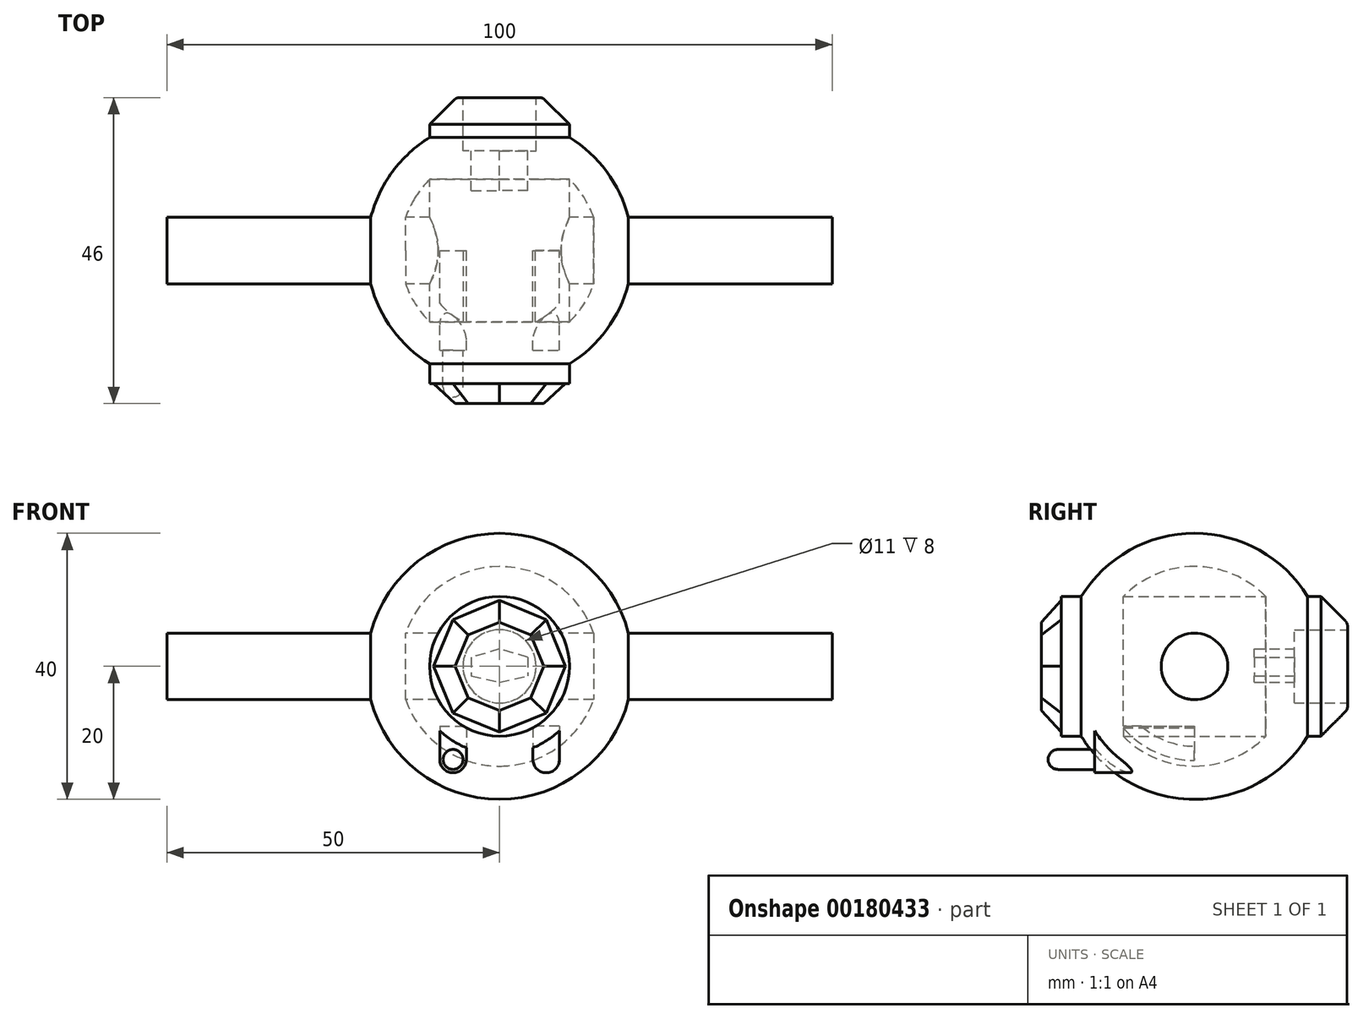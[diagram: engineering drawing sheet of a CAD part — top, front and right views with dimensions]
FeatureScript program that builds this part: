
annotation { "Feature Type Name" : "Feature", "Feature Type Description" : "" }
export const myFeature = defineFeature(function(context is Context, id is Id, definition is map)
    precondition{}
    {
        {
            var Q0;
            Q0=qCreatedBy(makeId("Front.planeOp"),FACE);
            var sketch = newSketch(context, id + "F0", { "sketchPlane" : qUnion([Q0])});
            skArc(sketch, "E0", {"start": v(0, 20) * mm, "mid": v(-20, 0) * mm, "end": v(0, -20) * mm});
            skArc(sketch, "E1", {"start": v(0, 15) * mm, "mid": v(-15, 0) * mm, "end": v(0, -15) * mm});
            skLineSegment(sketch, "E2", {"start": v(0, 20) * mm, "end": v(0, 15) * mm});
            skLineSegment(sketch, "E3.trimOffspring", {"start": v(0, -15) * mm, "end": v(0, -20) * mm});
            skSolve(sketch);
        }
        {
            var Q0;
            Q0=makeQuery(id+"F0.imprint","IMPRINT",FACE,{"disambiguationData":[TD([[makeQuery(id+"F0.imprint","IMPRINT",EDGE,{"derivedFrom":sQuery(id+"F0.wireOp",EDGE,"E0")}),1.0]])]});
            var Q1;
            Q1=sQuery(id+"F0.wireOp",EDGE,"E2");
            revolve(context, id + "F1", {"entities" : qUnion([Q0]), "axis" : qUnion([Q1]), "revolveType" : RevolveType.FULL});
        }
        {
            var Q0;
            Q0=qCreatedBy(makeId("Front.planeOp"),FACE);
            var sketch = newSketch(context, id + "F2", { "sketchPlane" : qUnion([Q0])});
            skCircle(sketch, "E4.cCircle", {"center": v(0, 0) * mm, "radius": 9.9 * mm, "construction": true});
            skLineSegment(sketch, "E4.0", {"start": v(7, -7) * mm, "end": v(0, -9.9) * mm});
            skLineSegment(sketch, "E4.1", {"start": v(0, -9.9) * mm, "end": v(-7, -7) * mm});
            skLineSegment(sketch, "E4.2", {"start": v(-7, -7) * mm, "end": v(-9.9, 0) * mm});
            skLineSegment(sketch, "E4.3", {"start": v(-9.9, 0) * mm, "end": v(-7, 7) * mm});
            skLineSegment(sketch, "E4.4", {"start": v(-7, 7) * mm, "end": v(0, 9.9) * mm});
            skLineSegment(sketch, "E4.5", {"start": v(0, 9.9) * mm, "end": v(7, 7) * mm});
            skLineSegment(sketch, "E4.6", {"start": v(7, 7) * mm, "end": v(9.9, 0) * mm});
            skLineSegment(sketch, "E4.7", {"start": v(9.9, 0) * mm, "end": v(7, -7) * mm});
            skSolve(sketch);
        }
        {
            var Q0;
            Q0 = qSketchRegion(id + "F2", true);
            extrude(context, id + "F3", {"entities" : qUnion([Q0]), "operationType" : NewBodyOperationType.ADD, "depth" : 23 * mm});
        }
        {
            var Q0;
            Q0=makeQuery(id+"F3.opExtrude","CAP_EDGE",EDGE,{"disambiguationData":[OSD([sQuery(id+"F2.wireOp",EDGE,"E4.4")])],"isStart":false});
            var Q1;
            Q1=makeQuery(id+"F3.opExtrude","CAP_EDGE",EDGE,{"disambiguationData":[OSD([sQuery(id+"F2.wireOp",EDGE,"E4.5")])],"isStart":false});
            var Q2;
            Q2=makeQuery(id+"F3.opExtrude","CAP_EDGE",EDGE,{"disambiguationData":[OSD([sQuery(id+"F2.wireOp",EDGE,"E4.3")])],"isStart":false});
            var Q3;
            Q3=makeQuery(id+"F3.opExtrude","CAP_EDGE",EDGE,{"disambiguationData":[OSD([sQuery(id+"F2.wireOp",EDGE,"E4.2")])],"isStart":false});
            var Q4;
            Q4=makeQuery(id+"F3.opExtrude","CAP_EDGE",EDGE,{"disambiguationData":[OSD([sQuery(id+"F2.wireOp",EDGE,"E4.1")])],"isStart":false});
            var Q5;
            Q5=makeQuery(id+"F3.opExtrude","CAP_EDGE",EDGE,{"disambiguationData":[OSD([sQuery(id+"F2.wireOp",EDGE,"E4.0")])],"isStart":false});
            var Q6;
            Q6=makeQuery(id+"F3.opExtrude","CAP_EDGE",EDGE,{"disambiguationData":[OSD([sQuery(id+"F2.wireOp",EDGE,"E4.7")])],"isStart":false});
            var Q7;
            Q7=makeQuery(id+"F3.opExtrude","CAP_EDGE",EDGE,{"disambiguationData":[OSD([sQuery(id+"F2.wireOp",EDGE,"E4.6")])],"isStart":false});
            chamfer(context, id + "F4", {"entities" : qUnion([Q0, Q1, Q2, Q3, Q4, Q5, Q6, Q7]), "width" : 3 * mm, "tangentPropagation" : true});
        }
        {
            var Q0;
            Q0=qCreatedBy(makeId("Front.planeOp"),FACE);
            var sketch = newSketch(context, id + "F5", { "sketchPlane" : qUnion([Q0])});
            skCircle(sketch, "E5", {"center": v(0, 0) * mm, "radius": 10.5 * mm});
            skSolve(sketch);
        }
        {
            var Q0;
            Q0 = qSketchRegion(id + "F5", true);
            extrude(context, id + "F6", {"entities" : qUnion([Q0]), "operationType" : NewBodyOperationType.ADD, "depth" : 20 * mm});
        }
        {
            var Q0;
            Q0=qCreatedBy(makeId("Front.planeOp"),FACE);
            var sketch = newSketch(context, id + "F7", { "sketchPlane" : qUnion([Q0])});
            skCircle(sketch, "E6", {"center": v(0, 0) * mm, "radius": 10.5 * mm});
            skSolve(sketch);
        }
        {
            var Q0;
            Q0 = qSketchRegion(id + "F7", true);
            extrude(context, id + "F8", {"entities" : qUnion([Q0]), "operationType" : NewBodyOperationType.ADD, "oppositeDirection" : true, "depth" : 23 * mm});
        }
        {
            var Q0;
            Q0=makeQuery(id+"F8.opExtrude","CAP_EDGE",EDGE,{"disambiguationData":[OSD([sQuery(id+"F7.wireOp",EDGE,"E6")])],"isStart":false});
            chamfer(context, id + "F9", {"entities" : qUnion([Q0]), "width" : 4 * mm, "tangentPropagation" : true});
        }
        {
            var Q0;
            Q0=makeQuery(id+"F8.opExtrude","CAP_FACE",FACE,{"disambiguationData":[OSD([sQuery(id+"F7.wireOp",EDGE,"E6")])],"isStart":false});
            var sketch = newSketch(context, id + "F10", { "sketchPlane" : qUnion([Q0])});
            skCircle(sketch, "E7", {"center": v(0, 0) * mm, "radius": 5.5 * mm});
            skSolve(sketch);
        }
        {
            var Q0;
            {var subQ0=sQuery(id+"F7.wireOp",EDGE,"E6");Q0=makeQuery(id+"F9.opChamfer","BLEND_EDGE",EDGE,{"blendedFrom":[makeQuery(id+"F8.opExtrude","CAP_EDGE",EDGE,{"disambiguationData":[OSD([subQ0])],"isStart":false}),makeQuery(id+"F8.opExtrude","CAP_FACE",FACE,{"disambiguationData":[OSD([subQ0])],"isStart":false})],"blendedInto":[makeQuery(id+"F8.opExtrude","CAP_FACE",FACE,{"disambiguationData":[OSD([subQ0])],"isStart":false})]});}
            fillet(context, id + "F11", {"entities" : qUnion([Q0]), "radius" : 1 * mm, "tangentPropagation" : true, "allowEdgeOverflow" : false});
        }
        {
            var Q0;
            Q0=sQuery(id+"F10.wireOp",VERTEX,"E7.center");
            var Q1;
            Q1=makeQuery(id+"F1.opRevolve","SWEPT_BODY",BODY,{"disambiguationData":[OSD([sQuery(id+"F0.wireOp",EDGE,"E0"),sQuery(id+"F0.wireOp",EDGE,"E1"),sQuery(id+"F0.wireOp",EDGE,"E2"),sQuery(id+"F0.wireOp",EDGE,"E3.trimOffspring")])]});
            hole(context, id + "F12", {"style" : HoleStyle.SIMPLE, "endStyle" : HoleEndStyle.BLIND, "holeDiameter" : 11 * mm, "holeDepth" : 10 * mm, "startFromSketch" : true, "locations" : qUnion([Q0]), "scope" : qUnion([Q1])});
        }
        {
            var Q0;
            Q0=qCreatedBy(makeId("Front.planeOp"),FACE);
            var sketch = newSketch(context, id + "F13", { "sketchPlane" : qUnion([Q0])});
            skCircle(sketch, "E8", {"center": v(0, 0) * mm, "radius": 5.5 * mm});
            skSolve(sketch);
        }
        {
            var Q0;
            Q0 = qSketchRegion(id + "F13", true);
            extrude(context, id + "F14", {"entities" : qUnion([Q0]), "operationType" : NewBodyOperationType.ADD, "oppositeDirection" : true, "depth" : 15 * mm});
        }
        {
            var Q0;
            Q0=makeQuery(id+"F14.opExtrude","CAP_FACE",FACE,{"disambiguationData":[OSD([sQuery(id+"F13.wireOp",EDGE,"E8")])],"isStart":false});
            var sketch = newSketch(context, id + "F15", { "sketchPlane" : qUnion([Q0])});
            skLineSegment(sketch, "E9", {"start": v(-4.25, 1.35) * mm, "end": v(-4.25, -1.4) * mm});
            skLineSegment(sketch, "E10", {"start": v(4.25, 1.35) * mm, "end": v(4.25, -1.4) * mm});
            skLineSegment(sketch, "E11", {"start": v(-4.25, 1.35) * mm, "end": v(0, 2.6) * mm});
            skLineSegment(sketch, "E12", {"start": v(0, 2.6) * mm, "end": v(4.25, 1.35) * mm});
            skLineSegment(sketch, "E13", {"start": v(4.25, -1.4) * mm, "end": v(0, -2.4) * mm});
            skLineSegment(sketch, "E14", {"start": v(0, -2.4) * mm, "end": v(-4.25, -1.4) * mm});
            skPoint(sketch, "E15.end.orphan", {"position": v(4.25, 0) * mm});
            skPoint(sketch, "E15.start.orphan", {"position": v(-4.25, 0) * mm});
            skSolve(sketch);
        }
        {
            var Q0;
            Q0=makeQuery(id+"F15.imprint","IMPRINT",FACE,{"disambiguationData":[TD([[makeQuery(id+"F15.imprint","IMPRINT",EDGE,{"derivedFrom":sQuery(id+"F15.wireOp",EDGE,"E9")}),1.0]])]});
            extrude(context, id + "F16", {"entities" : qUnion([Q0]), "operationType" : NewBodyOperationType.ADD, "depth" : 1 * mm});
        }
        {
            var Q0;
            Q0=makeQuery(id+"F16.opExtrude","CAP_FACE",FACE,{"disambiguationData":[OSD([sQuery(id+"F15.wireOp",EDGE,"E9"),sQuery(id+"F15.wireOp",EDGE,"E10"),sQuery(id+"F15.wireOp",EDGE,"E11"),sQuery(id+"F15.wireOp",EDGE,"E12"),sQuery(id+"F15.wireOp",EDGE,"E13"),sQuery(id+"F15.wireOp",EDGE,"E14")])],"isStart":false});
            extrude(context, id + "F17", {"entities" : qUnion([Q0]), "operationType" : NewBodyOperationType.REMOVE, "oppositeDirection" : true, "depth" : 7 * mm});
        }
        {
            var Q0;
            Q0=qCreatedBy(makeId("Front.planeOp"),FACE);
            var sketch = newSketch(context, id + "F18", { "sketchPlane" : qUnion([Q0])});
            skLineSegment(sketch, "E16.bottom", {"start": v(-9, -9) * mm, "end": v(-5, -9) * mm});
            skLineSegment(sketch, "E16.top", {"start": v(-9, -16) * mm, "end": v(-5, -16) * mm});
            skLineSegment(sketch, "E16.left", {"start": v(-9, -9) * mm, "end": v(-9, -16) * mm});
            skLineSegment(sketch, "E16.right", {"start": v(-5, -9) * mm, "end": v(-5, -16) * mm});
            skLineSegment(sketch, "E17.MirrorCS", {"start": v(9, -9) * mm, "end": v(9, -16) * mm});
            skLineSegment(sketch, "E18.MirrorCS", {"start": v(9, -16) * mm, "end": v(5, -16) * mm});
            skLineSegment(sketch, "E19.MirrorCS", {"start": v(5, -9) * mm, "end": v(5, -16) * mm});
            skLineSegment(sketch, "E20.MirrorCS", {"start": v(9, -9) * mm, "end": v(5, -9) * mm});
            skSolve(sketch);
        }
        {
            var Q0;
            Q0=makeQuery(id+"F18.imprint","IMPRINT",FACE,{"disambiguationData":[TD([[makeQuery(id+"F18.imprint","IMPRINT",EDGE,{"derivedFrom":sQuery(id+"F18.wireOp",EDGE,"E16.bottom")}),-1.0]])]});
            var Q1;
            Q1=makeQuery(id+"F18.imprint","IMPRINT",FACE,{"disambiguationData":[TD([[makeQuery(id+"F18.imprint","IMPRINT",EDGE,{"derivedFrom":sQuery(id+"F18.wireOp",EDGE,"E17.MirrorCS")}),-1.0]])]});
            extrude(context, id + "F19", {"entities" : qUnion([Q0, Q1]), "operationType" : NewBodyOperationType.ADD, "depth" : 15 * mm});
        }
        {
            var Q0;
            Q0=makeQuery(id+"F19.opExtrude","SWEPT_EDGE",EDGE,{"disambiguationData":[OSD([sQuery(id+"F18.wireOp",EDGE,"E16.top"),sQuery(id+"F18.wireOp",EDGE,"E16.left")])]});
            var Q1;
            Q1=makeQuery(id+"F19.opExtrude","SWEPT_EDGE",EDGE,{"disambiguationData":[OSD([sQuery(id+"F18.wireOp",EDGE,"E16.top"),sQuery(id+"F18.wireOp",EDGE,"E16.right")])]});
            var Q2;
            Q2=makeQuery(id+"F19.opExtrude","SWEPT_EDGE",EDGE,{"disambiguationData":[OSD([sQuery(id+"F18.wireOp",EDGE,"E18.MirrorCS"),sQuery(id+"F18.wireOp",EDGE,"E19.MirrorCS")])]});
            var Q3;
            Q3=makeQuery(id+"F19.opExtrude","SWEPT_EDGE",EDGE,{"disambiguationData":[OSD([sQuery(id+"F18.wireOp",EDGE,"E17.MirrorCS"),sQuery(id+"F18.wireOp",EDGE,"E18.MirrorCS")])]});
            fillet(context, id + "F20", {"entities" : qUnion([Q0, Q1, Q2, Q3]), "radius" : 2 * mm, "tangentPropagation" : true, "allowEdgeOverflow" : false});
        }
        {
            var Q0;
            Q0=makeQuery(id+"F19.opExtrude","CAP_FACE",FACE,{"disambiguationData":[OSD([sQuery(id+"F18.wireOp",EDGE,"E16.bottom"),sQuery(id+"F18.wireOp",EDGE,"E16.top"),sQuery(id+"F18.wireOp",EDGE,"E16.left"),sQuery(id+"F18.wireOp",EDGE,"E16.right")])],"isStart":false});
            var sketch = newSketch(context, id + "F21", { "sketchPlane" : qUnion([Q0])});
            skCircle(sketch, "E21", {"center": v(-7, -14) * mm, "radius": 1.5 * mm});
            skCircle(sketch, "E22.MirrorC", {"center": v(7, -14) * mm, "radius": 1.5 * mm});
            skSolve(sketch);
        }
        {
            var Q0;
            Q0=makeQuery(id+"F21.imprint","IMPRINT",FACE,{"disambiguationData":[TD([[makeQuery(id+"F21.imprint","IMPRINT",EDGE,{"derivedFrom":sQuery(id+"F21.wireOp",EDGE,"E21")}),1.0]])]});
            var Q1;
            Q1=makeQuery(id+"F21.imprint","IMPRINT",FACE,{"disambiguationData":[TD([[makeQuery(id+"F21.imprint","IMPRINT",EDGE,{"derivedFrom":sQuery(id+"F21.wireOp",EDGE,"E22.MirrorC")}),-1.0]])]});
            extrude(context, id + "F22", {"entities" : qUnion([Q0, Q1]), "operationType" : NewBodyOperationType.ADD, "depth" : 7 * mm});
        }
        {
            var Q0;
            Q0=makeQuery(id+"F22.opExtrude","CAP_EDGE",EDGE,{"disambiguationData":[OSD([sQuery(id+"F21.wireOp",EDGE,"E21")])],"isStart":false});
            var Q1;
            Q1=makeQuery(id+"F22.opExtrude","CAP_EDGE",EDGE,{"disambiguationData":[OSD([sQuery(id+"F21.wireOp",EDGE,"E22.MirrorC")])],"isStart":false});
            fillet(context, id + "F23", {"entities" : qUnion([Q0, Q1]), "radius" : 1.5 * mm, "tangentPropagation" : true, "allowEdgeOverflow" : false});
        }
        {
            var Q0;
            Q0=qCreatedBy(makeId("Right.planeOp"),FACE);
            var sketch = newSketch(context, id + "F24", { "sketchPlane" : qUnion([Q0])});
            skCircle(sketch, "E23", {"center": v(0, 0) * mm, "radius": 5 * mm});
            skSolve(sketch);
        }
        {
            var Q0;
            Q0 = qSketchRegion(id + "F24", true);
            extrude(context, id + "F25", {"entities" : qUnion([Q0]), "operationType" : NewBodyOperationType.ADD, "endBound" : BoundingType.SYMMETRIC, "depth" : 100 * mm});
        }
    });
